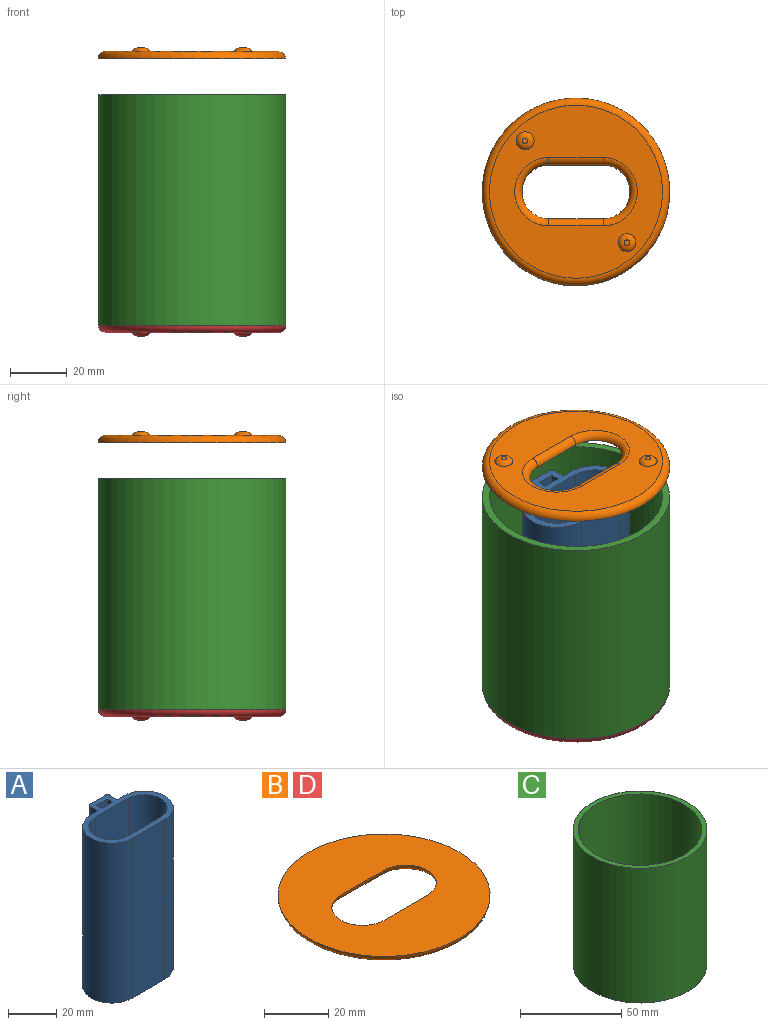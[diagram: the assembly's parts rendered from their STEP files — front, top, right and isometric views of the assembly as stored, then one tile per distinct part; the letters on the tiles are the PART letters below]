
ASSEMBLY  parts=4 mates=3
PART A: 20 faces, bbox 43.2x29.8x81.3 mm
  f0: plane 81.28x19.05mm, normal (0,1,0), area 1548.4mm2, adj f1,f17,f18,f19
  f1: cylinder r=9.53mm len=81.28mm, axis (0,0,-1), area 2432.2mm2, adj f0,f2,f18,f19
  f2: plane 81.28x19.05mm, normal (0,-1,0), area 1548.4mm2, adj f1,f17,f18,f19
  f3: plane 81.28x4.45mm, normal (1,0,0), area 361.3mm2, adj f4,f15,f18,f19
  f4: cylinder r=1.27mm len=81.28mm, axis (0,0,-1), area 162.1mm2, adj f3,f5,f18,f19
  f5: plane 81.28x8.89mm, normal (0,1,0), area 722.6mm2, adj f4,f6,f18,f19
  f6: cylinder r=1.27mm len=81.28mm, axis (0,0,-1), area 162.1mm2, adj f5,f7,f18,f19
  f7: plane 81.28x4.45mm, normal (-1,0,0), area 361.3mm2, adj f6,f8,f18,f19
  f8: plane 81.28x3.81mm, normal (0,1,0), area 309.7mm2, adj f7,f9,f18,f19
  f9: cylinder r=12.06mm len=81.28mm, axis (0,0,-1), area 3080.8mm2, adj f8,f10,f18,f19
  f10: plane 81.28x19.05mm, normal (0,-1,0), area 1548.4mm2, adj f9,f11,f18,f19
  f11: cylinder r=12.06mm len=81.28mm, axis (0,0,-1), area 3080.8mm2, adj f10,f15,f18,f19
  f12: plane 81.28x6.35mm, normal (0,1,0), area 516.1mm2, adj f13,f16,f18,f19
  f13: plane 81.28x3.18mm, normal (1,0,0), area 258.1mm2, adj f12,f14,f18,f19
  f14: plane 81.28x6.35mm, normal (0,-1,0), area 516.1mm2, adj f13,f16,f18,f19
  f15: plane 81.28x3.81mm, normal (0,1,0), area 309.7mm2, adj f3,f11,f18,f19
  f16: plane 81.28x3.18mm, normal (-1,0,0), area 258.1mm2, adj f12,f14,f18,f19
  f17: cylinder r=9.53mm len=81.28mm, axis (0,0,-1), area 2432.2mm2, adj f0,f2,f18,f19
  f18: plane 43.18x29.85mm, normal (0,0,1), area 313.5mm2, adj f0,f1,f2,f3,f4,f5,f6,f7
  f19: plane 43.18x29.85mm, normal (0,0,-1), area 313.5mm2, adj f0,f1,f2,f3,f4,f5,f6,f7
PART B: 11 faces, bbox 71.5x71.5x5.6 mm
  f0: plane 66.04x66.04mm, normal (0,0,1), area 2777.4mm2, adj f4,f5,f6,f7,f10
  f1: plane 60.96x60.96mm, normal (0,0,-1), area 1938.3mm2, adj f4,f5,f6,f7,f8,f9,f10
  f2: plane 1.95x1.95mm, normal (0,0,-1), area 3mm2, adj f9
  f3: plane 1.95x1.95mm, normal (0,0,-1), area 3mm2, adj f8
  f4: torus R=12.06mm, axis (0,0,1), area 131mm2, adj f0,f1,f5,f6
  f5: cylinder r=2.54mm len=19.05mm, axis (1,0,0), area 76mm2, adj f0,f1,f4,f7
  f6: cylinder r=2.54mm len=19.05mm, axis (-1,0,0), area 76mm2, adj f0,f1,f4,f7
  f7: torus R=12.06mm, axis (0,0,1), area 131mm2, adj f0,f1,f5,f6
  f8: torus R=0.98mm, axis (0,0,-1), area 36.6mm2, adj f1,f3
  f9: torus R=0.98mm, axis (0,0,-1), area 36.6mm2, adj f1,f2
  f10: torus R=30.48mm, axis (0,0,1), area 804.6mm2, adj f0,f1
PART C: 4 faces, bbox 66x66x81.3 mm
  f0: cylinder r=30.48mm len=81.28mm, axis (0,0,-1), area 15566.1mm2, adj f2,f3
  f1: cylinder r=33.02mm len=81.28mm, axis (0,0,-1), area 16863.2mm2, adj f2,f3
  f2: plane 66.04x66.04mm, normal (0,0,1), area 506.7mm2, adj f0,f1
  f3: plane 66.04x66.04mm, normal (0,0,-1), area 506.7mm2, adj f0,f1
PART D: same geometry as B
PLACE A t=(-238.21,-23.67,-101.78)mm
PLACE B rot(axis=(0,-1,0),180deg) t=(-200.72,62.23,-5.26)mm
PLACE C t=(-106.58,-14.66,-101.78)mm
PLACE D t=(-208.1,62.23,-104.32)mm
MATE fastened A.f19 <-> D.f0  axis (0,0,-1) through (-204.41,0.69,-101.78)mm
MATE fastened C.f0 <-> B.f10  axis (0,0,1) through (-204.41,10.22,-20.5)mm
MATE fastened C.f0 <-> D.f10  axis (0,0,-1) through (-204.41,10.22,-101.78)mm
